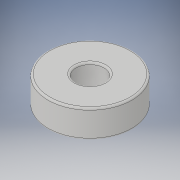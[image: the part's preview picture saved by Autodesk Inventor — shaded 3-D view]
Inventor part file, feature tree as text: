
AUTODESK INVENTOR PART (.ipt)
format: ipt  version: 2018 (Build 220112000, 112)  size: 134,144 bytes
history: native  units: in
note: dims shown in document units (in); Inventor stores cm internally (conversion verified against a paired STEP export)
features: fillet x4, extrude x1, sketch x1
ambient origin geometry x8: Origin, YZ Plane, XZ Plane, XY Plane, X Axis, Y Axis, Z Axis, Center Point
bodies: Solid1 (feature_tree)
feature tree (6):
  extrude  "Extrusion1"  Depth=0.025in
  fillet  "Fillet1"  Radius=0.375in
  fillet  "Fillet2"  Radius=0.025in
  fillet  "Fillet3"  Radius=0.025in
  fillet  "Fillet4"  Radius=0.025in
  sketch  "Sketch1"  dims[d0=0.375in d1=1.125in d2=0.375in d3=0.0in d4=0.025in d5=0.025in d6=0.025in d7=0.025in]
